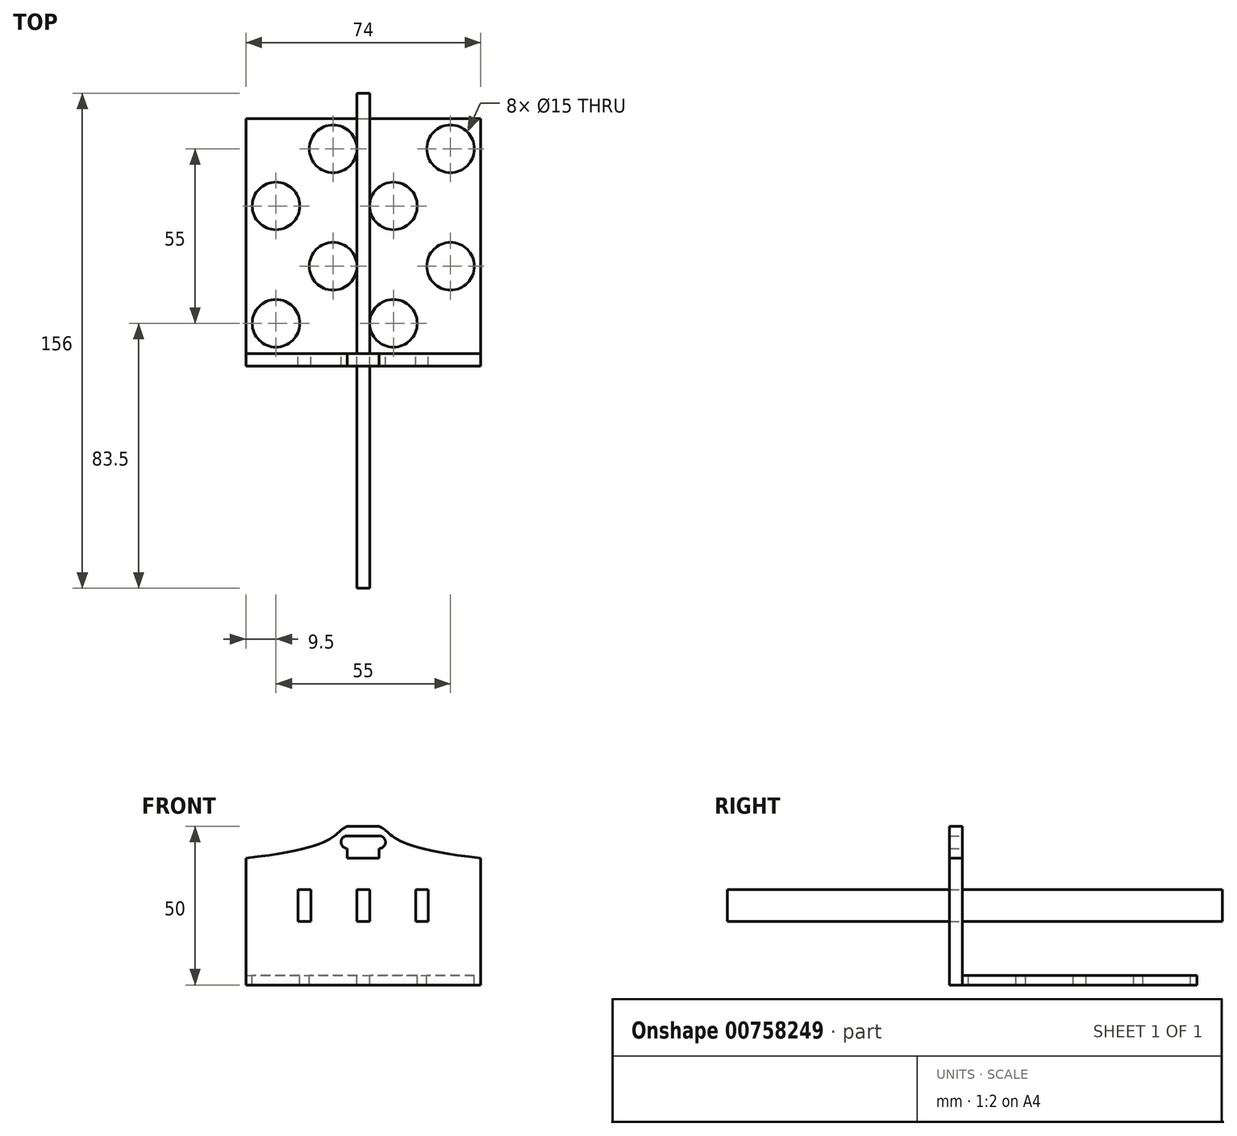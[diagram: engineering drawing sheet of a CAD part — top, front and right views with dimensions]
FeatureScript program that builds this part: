
annotation { "Feature Type Name" : "Feature", "Feature Type Description" : "" }
export const myFeature = defineFeature(function(context is Context, id is Id, definition is map)
    precondition{}
    {
        {
            assignVariable(context, id + "F0", {"name" : "ToteLength", "anyValue" : 37 * 2});
        }
        {
            var Q0;
            Q0=qCreatedBy(makeId("Top.planeOp"),FACE);
            var sketch = newSketch(context, id + "F1", { "sketchPlane" : qUnion([Q0])});
            skLineSegment(sketch, "E0.bottom", {"start": v(-37, 37) * mm, "end": v(37, 37) * mm});
            skLineSegment(sketch, "E0.top", {"start": v(-37, -37) * mm, "end": v(37, -37) * mm});
            skLineSegment(sketch, "E0.left", {"start": v(-37, 37) * mm, "end": v(-37, -37) * mm});
            skLineSegment(sketch, "E0.right", {"start": v(37, 37) * mm, "end": v(37, -37) * mm});
            skLineSegment(sketch, "E1", {"start": v(-43.8, 0) * mm, "end": v(54.1, 0) * mm, "construction": true});
            skLineSegment(sketch, "E2", {"start": v(0, -45.96) * mm, "end": v(0, 71.87) * mm, "construction": true});
            skPoint(sketch, "E2.endSnap0", {"position": v(0, 37) * mm});
            skCircle(sketch, "E3", {"center": v(-27.5, 27.5) * mm, "radius": 7.5 * mm});
            skCircle(sketch, "E4.MirrorC", {"center": v(27.5, 27.5) * mm, "radius": 7.5 * mm});
            skCircle(sketch, "E5.MirrorC", {"center": v(27.5, -27.5) * mm, "radius": 7.5 * mm});
            skCircle(sketch, "E6.MirrorC", {"center": v(-27.5, -27.5) * mm, "radius": 7.5 * mm});
            skLineSegment(sketch, "E7", {"start": v(-18.5, 47.73) * mm, "end": v(-18.5, -48.1) * mm, "construction": true});
            skLineSegment(sketch, "E8.MirrorCS", {"start": v(18.5, 47.73) * mm, "end": v(18.5, -48.1) * mm, "construction": true});
            skLineSegment(sketch, "E9", {"start": v(-48.14, 18.5) * mm, "end": v(59.01, 18.5) * mm, "construction": true});
            skLineSegment(sketch, "E10.MirrorCS", {"start": v(-43.8, 37) * mm, "end": v(54.1, 37) * mm, "construction": true});
            skLineSegment(sketch, "E11.MirrorCS", {"start": v(-48.14, -18.5) * mm, "end": v(59.01, -18.5) * mm, "construction": true});
            skCircle(sketch, "E12.MirrorC", {"center": v(-27.5, 9.5) * mm, "radius": 7.5 * mm});
            skCircle(sketch, "E13.MirrorC", {"center": v(-27.5, -9.5) * mm, "radius": 7.5 * mm});
            skCircle(sketch, "E14.MirrorC", {"center": v(27.5, -9.5) * mm, "radius": 7.5 * mm});
            skCircle(sketch, "E15.MirrorC", {"center": v(-9.5, 27.5) * mm, "radius": 7.5 * mm});
            skCircle(sketch, "E16.MirrorC", {"center": v(-9.5, 9.5) * mm, "radius": 7.5 * mm});
            skCircle(sketch, "E17.MirrorC", {"center": v(-9.5, -9.5) * mm, "radius": 7.5 * mm});
            skCircle(sketch, "E18.MirrorC", {"center": v(-9.5, -27.5) * mm, "radius": 7.5 * mm});
            skCircle(sketch, "E19.MirrorC", {"center": v(27.5, 9.5) * mm, "radius": 7.5 * mm});
            skCircle(sketch, "E20.MirrorC", {"center": v(9.5, 27.5) * mm, "radius": 7.5 * mm});
            skCircle(sketch, "E21.MirrorC", {"center": v(9.5, 9.5) * mm, "radius": 7.5 * mm});
            skCircle(sketch, "E22.MirrorC", {"center": v(9.5, -9.5) * mm, "radius": 7.5 * mm});
            skCircle(sketch, "E23.MirrorC", {"center": v(9.5, -27.5) * mm, "radius": 7.5 * mm});
            skSolve(sketch);
        }
        {
            var Q0;
            Q0 = qSketchRegion(id + "F1", true);
            var Q1;
            Q1=makeQuery(id+"F1.imprint","IMPRINT",FACE,{"disambiguationData":[TD([[makeQuery(id+"F1.imprint","IMPRINT",EDGE,{"derivedFrom":sQuery(id+"F1.wireOp",EDGE,"E3")}),1.0]])]});
            var Q2;
            Q2=makeQuery(id+"F1.imprint","IMPRINT",FACE,{"disambiguationData":[TD([[makeQuery(id+"F1.imprint","IMPRINT",EDGE,{"derivedFrom":sQuery(id+"F1.wireOp",EDGE,"E6.MirrorC")}),-1.0]])]});
            var Q3;
            Q3=makeQuery(id+"F1.imprint","IMPRINT",FACE,{"disambiguationData":[TD([[makeQuery(id+"F1.imprint","IMPRINT",EDGE,{"derivedFrom":sQuery(id+"F1.wireOp",EDGE,"E4.MirrorC")}),-1.0]])]});
            var Q4;
            Q4=makeQuery(id+"F1.imprint","IMPRINT",FACE,{"disambiguationData":[TD([[makeQuery(id+"F1.imprint","IMPRINT",EDGE,{"derivedFrom":sQuery(id+"F1.wireOp",EDGE,"E5.MirrorC")}),1.0]])]});
            var Q5;
            Q5=makeQuery(id+"F1.imprint","IMPRINT",FACE,{"disambiguationData":[TD([[makeQuery(id+"F1.imprint","IMPRINT",EDGE,{"derivedFrom":sQuery(id+"F1.wireOp",EDGE,"E13.MirrorC")}),1.0]])]});
            var Q6;
            Q6=makeQuery(id+"F1.imprint","IMPRINT",FACE,{"disambiguationData":[TD([[makeQuery(id+"F1.imprint","IMPRINT",EDGE,{"derivedFrom":sQuery(id+"F1.wireOp",EDGE,"E12.MirrorC")}),-1.0]])]});
            var Q7;
            Q7=makeQuery(id+"F1.imprint","IMPRINT",FACE,{"disambiguationData":[TD([[makeQuery(id+"F1.imprint","IMPRINT",EDGE,{"derivedFrom":sQuery(id+"F1.wireOp",EDGE,"E15.MirrorC")}),-1.0]])]});
            var Q8;
            Q8=makeQuery(id+"F1.imprint","IMPRINT",FACE,{"disambiguationData":[TD([[makeQuery(id+"F1.imprint","IMPRINT",EDGE,{"derivedFrom":sQuery(id+"F1.wireOp",EDGE,"E16.MirrorC")}),1.0]])]});
            var Q9;
            Q9=makeQuery(id+"F1.imprint","IMPRINT",FACE,{"disambiguationData":[TD([[makeQuery(id+"F1.imprint","IMPRINT",EDGE,{"derivedFrom":sQuery(id+"F1.wireOp",EDGE,"E17.MirrorC")}),-1.0]])]});
            var Q10;
            Q10=makeQuery(id+"F1.imprint","IMPRINT",FACE,{"disambiguationData":[TD([[makeQuery(id+"F1.imprint","IMPRINT",EDGE,{"derivedFrom":sQuery(id+"F1.wireOp",EDGE,"E18.MirrorC")}),1.0]])]});
            var Q11;
            Q11=makeQuery(id+"F1.imprint","IMPRINT",FACE,{"disambiguationData":[TD([[makeQuery(id+"F1.imprint","IMPRINT",EDGE,{"derivedFrom":sQuery(id+"F1.wireOp",EDGE,"E23.MirrorC")}),-1.0]])]});
            var Q12;
            Q12=makeQuery(id+"F1.imprint","IMPRINT",FACE,{"disambiguationData":[TD([[makeQuery(id+"F1.imprint","IMPRINT",EDGE,{"derivedFrom":sQuery(id+"F1.wireOp",EDGE,"E22.MirrorC")}),1.0]])]});
            var Q13;
            Q13=makeQuery(id+"F1.imprint","IMPRINT",FACE,{"disambiguationData":[TD([[makeQuery(id+"F1.imprint","IMPRINT",EDGE,{"derivedFrom":sQuery(id+"F1.wireOp",EDGE,"E21.MirrorC")}),-1.0]])]});
            var Q14;
            Q14=makeQuery(id+"F1.imprint","IMPRINT",FACE,{"disambiguationData":[TD([[makeQuery(id+"F1.imprint","IMPRINT",EDGE,{"derivedFrom":sQuery(id+"F1.wireOp",EDGE,"E20.MirrorC")}),1.0]])]});
            var Q15;
            Q15=makeQuery(id+"F1.imprint","IMPRINT",FACE,{"disambiguationData":[TD([[makeQuery(id+"F1.imprint","IMPRINT",EDGE,{"derivedFrom":sQuery(id+"F1.wireOp",EDGE,"E14.MirrorC")}),-1.0]])]});
            var Q16;
            Q16=makeQuery(id+"F1.imprint","IMPRINT",FACE,{"disambiguationData":[TD([[makeQuery(id+"F1.imprint","IMPRINT",EDGE,{"derivedFrom":sQuery(id+"F1.wireOp",EDGE,"E19.MirrorC")}),1.0]])]});
            extrude(context, id + "F2", {"entities" : qUnion([Q0, Q1, Q2, Q3, Q4, Q5, Q6, Q7, Q8, Q9, Q10, Q11, Q12, Q13, Q14, Q15, Q16]), "oppositeDirection" : true, "depth" : 7 * mm, "offsetDistance" : 25 * mm});
        }
        {
            var Q0;
            Q0=makeQuery(id+"F1.imprint","IMPRINT",FACE,{"disambiguationData":[TD([[makeQuery(id+"F1.imprint","IMPRINT",EDGE,{"derivedFrom":sQuery(id+"F1.wireOp",EDGE,"E6.MirrorC")}),-1.0]])]});
            var Q1;
            Q1=makeQuery(id+"F1.imprint","IMPRINT",FACE,{"disambiguationData":[TD([[makeQuery(id+"F1.imprint","IMPRINT",EDGE,{"derivedFrom":sQuery(id+"F1.wireOp",EDGE,"E3")}),1.0]])]});
            var Q2;
            Q2=makeQuery(id+"F1.imprint","IMPRINT",FACE,{"disambiguationData":[TD([[makeQuery(id+"F1.imprint","IMPRINT",EDGE,{"derivedFrom":sQuery(id+"F1.wireOp",EDGE,"E4.MirrorC")}),-1.0]])]});
            var Q3;
            Q3=makeQuery(id+"F1.imprint","IMPRINT",FACE,{"disambiguationData":[TD([[makeQuery(id+"F1.imprint","IMPRINT",EDGE,{"derivedFrom":sQuery(id+"F1.wireOp",EDGE,"E5.MirrorC")}),1.0]])]});
            var Q4;
            Q4=makeQuery(id+"F1.imprint","IMPRINT",FACE,{"disambiguationData":[TD([[makeQuery(id+"F1.imprint","IMPRINT",EDGE,{"derivedFrom":sQuery(id+"F1.wireOp",EDGE,"E13.MirrorC")}),1.0]])]});
            var Q5;
            Q5=makeQuery(id+"F1.imprint","IMPRINT",FACE,{"disambiguationData":[TD([[makeQuery(id+"F1.imprint","IMPRINT",EDGE,{"derivedFrom":sQuery(id+"F1.wireOp",EDGE,"E12.MirrorC")}),-1.0]])]});
            var Q6;
            Q6=makeQuery(id+"F1.imprint","IMPRINT",FACE,{"disambiguationData":[TD([[makeQuery(id+"F1.imprint","IMPRINT",EDGE,{"derivedFrom":sQuery(id+"F1.wireOp",EDGE,"E18.MirrorC")}),1.0]])]});
            var Q7;
            Q7=makeQuery(id+"F1.imprint","IMPRINT",FACE,{"disambiguationData":[TD([[makeQuery(id+"F1.imprint","IMPRINT",EDGE,{"derivedFrom":sQuery(id+"F1.wireOp",EDGE,"E17.MirrorC")}),-1.0]])]});
            var Q8;
            Q8=makeQuery(id+"F1.imprint","IMPRINT",FACE,{"disambiguationData":[TD([[makeQuery(id+"F1.imprint","IMPRINT",EDGE,{"derivedFrom":sQuery(id+"F1.wireOp",EDGE,"E16.MirrorC")}),1.0]])]});
            var Q9;
            Q9=makeQuery(id+"F1.imprint","IMPRINT",FACE,{"disambiguationData":[TD([[makeQuery(id+"F1.imprint","IMPRINT",EDGE,{"derivedFrom":sQuery(id+"F1.wireOp",EDGE,"E15.MirrorC")}),-1.0]])]});
            var Q10;
            Q10=makeQuery(id+"F1.imprint","IMPRINT",FACE,{"disambiguationData":[TD([[makeQuery(id+"F1.imprint","IMPRINT",EDGE,{"derivedFrom":sQuery(id+"F1.wireOp",EDGE,"E20.MirrorC")}),1.0]])]});
            var Q11;
            Q11=makeQuery(id+"F1.imprint","IMPRINT",FACE,{"disambiguationData":[TD([[makeQuery(id+"F1.imprint","IMPRINT",EDGE,{"derivedFrom":sQuery(id+"F1.wireOp",EDGE,"E21.MirrorC")}),-1.0]])]});
            var Q12;
            Q12=makeQuery(id+"F1.imprint","IMPRINT",FACE,{"disambiguationData":[TD([[makeQuery(id+"F1.imprint","IMPRINT",EDGE,{"derivedFrom":sQuery(id+"F1.wireOp",EDGE,"E22.MirrorC")}),1.0]])]});
            var Q13;
            Q13=makeQuery(id+"F1.imprint","IMPRINT",FACE,{"disambiguationData":[TD([[makeQuery(id+"F1.imprint","IMPRINT",EDGE,{"derivedFrom":sQuery(id+"F1.wireOp",EDGE,"E23.MirrorC")}),-1.0]])]});
            var Q14;
            Q14=makeQuery(id+"F1.imprint","IMPRINT",FACE,{"disambiguationData":[TD([[makeQuery(id+"F1.imprint","IMPRINT",EDGE,{"derivedFrom":sQuery(id+"F1.wireOp",EDGE,"E14.MirrorC")}),-1.0]])]});
            var Q15;
            Q15=makeQuery(id+"F1.imprint","IMPRINT",FACE,{"disambiguationData":[TD([[makeQuery(id+"F1.imprint","IMPRINT",EDGE,{"derivedFrom":sQuery(id+"F1.wireOp",EDGE,"E19.MirrorC")}),1.0]])]});
            extrude(context, id + "F3", {"entities" : qUnion([Q0, Q1, Q2, Q3, Q4, Q5, Q6, Q7, Q8, Q9, Q10, Q11, Q12, Q13, Q14, Q15]), "operationType" : NewBodyOperationType.REMOVE, "oppositeDirection" : true, "depth" : 4 * mm, "offsetDistance" : 25 * mm});
        }
        {
            var Q0;
            Q0=makeQuery(id+"F2.opExtrude","SWEPT_FACE",FACE,{"disambiguationData":[OSD([sQuery(id+"F1.wireOp",EDGE,"E0.top")])]});
            var sketch = newSketch(context, id + "F4", { "sketchPlane" : qUnion([Q0])});
            skLineSegment(sketch, "E24.bottom", {"start": v(-37, -7) * mm, "end": v(37, -7) * mm});
            skLineSegment(sketch, "E24.top", {"start": v(-37, 33) * mm, "end": v(37, 33) * mm});
            skLineSegment(sketch, "E24.left", {"start": v(-37, -7) * mm, "end": v(-37, 33) * mm});
            skLineSegment(sketch, "E24.right", {"start": v(37, -7) * mm, "end": v(37, 33) * mm});
            skLineSegment(sketch, "E25.bottom", {"start": v(-5, 33) * mm, "end": v(5, 33) * mm});
            skLineSegment(sketch, "E25.top", {"start": v(-5, 43) * mm, "end": v(5, 43) * mm});
            skLineSegment(sketch, "E25.left", {"start": v(-5, 33) * mm, "end": v(-5, 43) * mm});
            skLineSegment(sketch, "E25.right", {"start": v(5, 33) * mm, "end": v(5, 43) * mm});
            skFitSpline(sketch, "E26", {"points": [v(-37, 33) * mm, v(-5, 43) * mm], "startDerivative": vector(91.97, 9.82) * mm, "endDerivative": vector(12.88, 4.34) * mm});
            skFitSpline(sketch, "E27.MirrorCS", {"points": [v(37, 33) * mm, v(5, 43) * mm], "startDerivative": vector(-91.97, 9.82) * mm, "endDerivative": vector(-12.88, 4.34) * mm});
            skCircle(sketch, "E28", {"center": v(-5, 38) * mm, "radius": 2 * mm});
            skCircle(sketch, "E29", {"center": v(5, 38) * mm, "radius": 2 * mm});
            skLineSegment(sketch, "E30", {"start": v(-5, 36) * mm, "end": v(5, 36) * mm});
            skLineSegment(sketch, "E31", {"start": v(-5, 40) * mm, "end": v(5, 40) * mm});
            skLineSegment(sketch, "E32.bottom", {"start": v(-2, 23) * mm, "end": v(2, 23) * mm});
            skLineSegment(sketch, "E32.top", {"start": v(-2, 13) * mm, "end": v(2, 13) * mm});
            skLineSegment(sketch, "E32.left", {"start": v(-2, 23) * mm, "end": v(-2, 13) * mm});
            skLineSegment(sketch, "E32.right", {"start": v(2, 23) * mm, "end": v(2, 13) * mm});
            skLineSegment(sketch, "E33", {"start": v(-18.5, -18.16) * mm, "end": v(-18.5, 48.33) * mm, "construction": true});
            skLineSegment(sketch, "E34", {"start": v(18.5, -16.34) * mm, "end": v(18.5, 49.66) * mm, "construction": true});
            skLineSegment(sketch, "E35.bottom", {"start": v(-20.5, 23) * mm, "end": v(-16.5, 23) * mm});
            skLineSegment(sketch, "E35.top", {"start": v(-20.5, 13) * mm, "end": v(-16.5, 13) * mm});
            skLineSegment(sketch, "E35.left", {"start": v(-20.5, 23) * mm, "end": v(-20.5, 13) * mm});
            skLineSegment(sketch, "E35.right", {"start": v(-16.5, 23) * mm, "end": v(-16.5, 13) * mm});
            skLineSegment(sketch, "E36", {"start": v(30, 23) * mm, "end": v(-68.16, 23) * mm, "construction": true});
            skLineSegment(sketch, "E37.MirrorCS", {"start": v(20.5, 13) * mm, "end": v(16.5, 13) * mm});
            skLineSegment(sketch, "E38.MirrorCS", {"start": v(16.5, 23) * mm, "end": v(16.5, 13) * mm});
            skLineSegment(sketch, "E39.MirrorCS", {"start": v(20.5, 23) * mm, "end": v(20.5, 13) * mm});
            skLineSegment(sketch, "E40.MirrorCS", {"start": v(20.5, 23) * mm, "end": v(16.5, 23) * mm});
            skSolve(sketch);
        }
        {
            var Q0;
            Q0 = qSketchRegion(id + "F4", true);
            var Q1;
            {var subQ0=sQuery(id+"F4.wireOp",EDGE,"E25.bottom");Q1=makeQuery(id+"F4.imprint","IMPRINT",FACE,{"disambiguationData":[TD([[makeQuery(id+"F4.imprint","IMPRINT",EDGE,{"derivedFrom":subQ0}),1.0]])]});}
            extrude(context, id + "F5", {"entities" : qUnion([Q0, Q1]), "depth" : 4 * mm, "offsetDistance" : 25 * mm});
        }
        {
            var Q0;
            Q0=makeQuery(id+"F4.imprint","IMPRINT",FACE,{"disambiguationData":[TD([[makeQuery(id+"F4.imprint","IMPRINT",EDGE,{"derivedFrom":sQuery(id+"F4.wireOp",EDGE,"E32.bottom")}),-1.0]])]});
            extrude(context, id + "F6", {"entities" : qUnion([Q0]), "operationType" : NewBodyOperationType.ADD, "oppositeDirection" : true, "depth" : (getVariable(context, 'ToteLength') + (2 * 4)) * mm, "offsetDistance" : 25 * mm});
        }
        {
            var Q0;
            Q0=makeQuery(id+"F4.imprint","IMPRINT",FACE,{"disambiguationData":[TD([[makeQuery(id+"F4.imprint","IMPRINT",EDGE,{"derivedFrom":sQuery(id+"F4.wireOp",EDGE,"E32.bottom")}),-1.0]])]});
            extrude(context, id + "F7", {"entities" : qUnion([Q0]), "depth" : (getVariable(context, 'ToteLength')) * mm, "offsetDistance" : 25 * mm});
        }
    });
